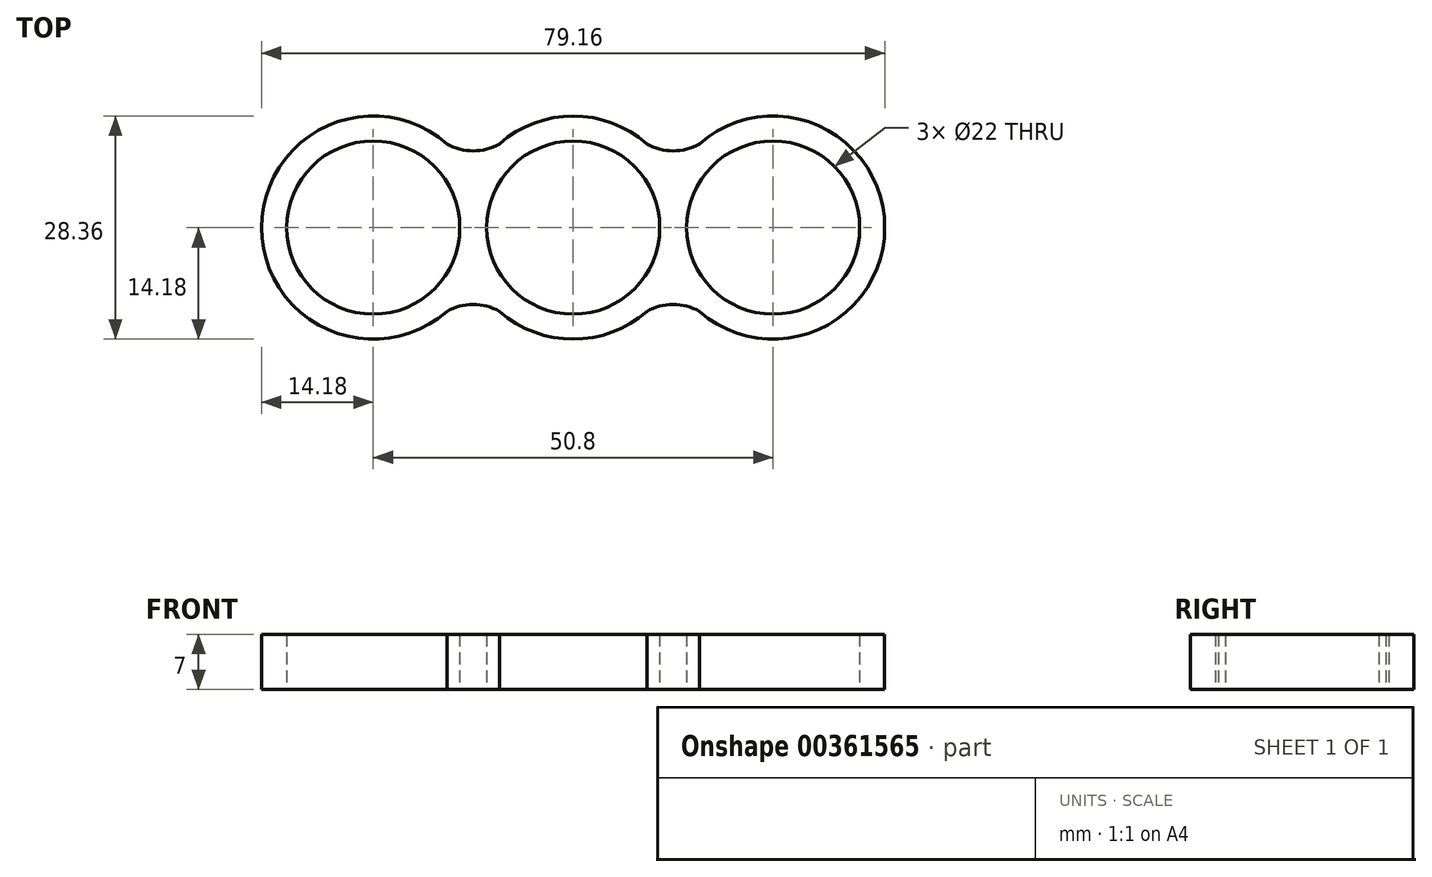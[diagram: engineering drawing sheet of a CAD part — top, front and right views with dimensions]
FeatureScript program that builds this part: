
annotation { "Feature Type Name" : "Feature", "Feature Type Description" : "" }
export const myFeature = defineFeature(function(context is Context, id is Id, definition is map)
    precondition{}
    {
        {
            var Q0;
            Q0=qCreatedBy(makeId("Top.planeOp"),FACE);
            var sketch = newSketch(context, id + "F0", { "sketchPlane" : qUnion([Q0])});
            skCircle(sketch, "E0", {"center": v(0, 0) * mm, "radius": 11 * mm});
            skCircle(sketch, "E1", {"center": v(0, 0) * mm, "radius": 14.17 * mm});
            skLineSegment(sketch, "E2", {"start": v(0, 0) * mm, "end": v(-25.4, 0) * mm});
            skLineSegment(sketch, "E3", {"start": v(0, 0) * mm, "end": v(25.4, 0) * mm});
            skCircle(sketch, "E4", {"center": v(-25.4, 0) * mm, "radius": 11 * mm});
            skCircle(sketch, "E5", {"center": v(25.4, 0) * mm, "radius": 11 * mm});
            skCircle(sketch, "E6", {"center": v(25.4, 0) * mm, "radius": 14.17 * mm});
            skCircle(sketch, "E7", {"center": v(-25.4, 0) * mm, "radius": 14.17 * mm});
            skPoint(sketch, "E8", {"position": v(-16.02, 10.63) * mm});
            skPoint(sketch, "E9", {"position": v(-9.36, 10.64) * mm});
            skPoint(sketch, "E10", {"position": v(16.04, -10.64) * mm});
            skPoint(sketch, "E11", {"position": v(9.36, -10.64) * mm});
            skPoint(sketch, "E12", {"position": v(-12.7, 9.74) * mm});
            skArc(sketch, "E13", {"start": v(-16.02, 10.63) * mm, "mid": v(-12.7, 9.74) * mm, "end": v(-9.36, 10.64) * mm});
            skPoint(sketch, "E14", {"position": v(9.36, 10.64) * mm});
            skPoint(sketch, "E15", {"position": v(16.04, 10.64) * mm});
            skPoint(sketch, "E16", {"position": v(12.7, -9.75) * mm});
            skPoint(sketch, "E17", {"position": v(12.7, 9.75) * mm});
            skPoint(sketch, "E18", {"position": v(-16.04, -10.64) * mm});
            skPoint(sketch, "E19", {"position": v(-9.36, -10.64) * mm});
            skPoint(sketch, "E20", {"position": v(-12.7, -9.75) * mm});
            skArc(sketch, "E21", {"start": v(-9.36, -10.64) * mm, "mid": v(-12.7, -9.75) * mm, "end": v(-16.04, -10.64) * mm});
            skArc(sketch, "E22", {"start": v(16.04, -10.64) * mm, "mid": v(12.7, -9.75) * mm, "end": v(9.36, -10.64) * mm});
            skArc(sketch, "E23", {"start": v(9.36, 10.64) * mm, "mid": v(12.7, 9.75) * mm, "end": v(16.04, 10.64) * mm});
            skSolve(sketch);
        }
        {
            var Q0;
            Q0=makeQuery(id+"F0.imprint","IMPRINT",FACE,{"disambiguationData":[TD([[makeQuery(id+"F0.imprint","IMPRINT",EDGE,{"derivedFrom":sQuery(id+"F0.wireOp",EDGE,"E4")}),-1.0]])]});
            var Q1;
            {var subQ7=sQuery(id+"F0.wireOp",EDGE,"E2");var subQ10=sQuery(id+"F0.wireOp",EDGE,"E0");var subQ13=makeQuery(id+"F0.imprint","INTERSECT",VERTEX,{"derivedFrom":[subQ10,subQ7]});Q1=makeQuery(id+"F0.imprint","IMPRINT",FACE,{"disambiguationData":[TD([[makeQuery(id+"F0.imprint","IMPRINT",EDGE,{"disambiguationData":[TD([[subQ13,1.0]])],"derivedFrom":subQ10}),-1.0]])]});}
            var Q2;
            {var subQ0=sQuery(id+"F0.wireOp",EDGE,"E13");Q2=makeQuery(id+"F0.imprint","IMPRINT",FACE,{"disambiguationData":[TD([[makeQuery(id+"F0.imprint","IMPRINT",EDGE,{"derivedFrom":subQ0}),-1.0]])]});}
            var Q3;
            {var subQ0=sQuery(id+"F0.wireOp",EDGE,"E2");var subQ1=sQuery(id+"F0.wireOp",EDGE,"E1");var subQ2=makeQuery(id+"F0.imprint","INTERSECT",VERTEX,{"derivedFrom":[subQ1,subQ0]});Q3=makeQuery(id+"F0.imprint","IMPRINT",FACE,{"disambiguationData":[TD([[makeQuery(id+"F0.imprint","IMPRINT",EDGE,{"disambiguationData":[TD([[subQ2,1.0]])],"derivedFrom":subQ1}),1.0]])]});}
            var Q4;
            {var subQ0=sQuery(id+"F0.wireOp",EDGE,"E2");var subQ1=sQuery(id+"F0.wireOp",EDGE,"E1");var subQ2=makeQuery(id+"F0.imprint","INTERSECT",VERTEX,{"derivedFrom":[subQ1,subQ0]});Q4=makeQuery(id+"F0.imprint","IMPRINT",FACE,{"disambiguationData":[TD([[makeQuery(id+"F0.imprint","IMPRINT",EDGE,{"disambiguationData":[TD([[subQ2,-1.0]])],"derivedFrom":subQ1}),1.0]])]});}
            var Q5;
            {var subQ7=sQuery(id+"F0.wireOp",EDGE,"E2");var subQ8=sQuery(id+"F0.wireOp",EDGE,"E0");var subQ9=makeQuery(id+"F0.imprint","INTERSECT",VERTEX,{"derivedFrom":[subQ8,subQ7]});Q5=makeQuery(id+"F0.imprint","IMPRINT",FACE,{"disambiguationData":[TD([[makeQuery(id+"F0.imprint","IMPRINT",EDGE,{"disambiguationData":[TD([[subQ9,-1.0]])],"derivedFrom":subQ8}),-1.0]])]});}
            var Q6;
            {var subQ0=sQuery(id+"F0.wireOp",EDGE,"E21");Q6=makeQuery(id+"F0.imprint","IMPRINT",FACE,{"disambiguationData":[TD([[makeQuery(id+"F0.imprint","IMPRINT",EDGE,{"derivedFrom":subQ0}),-1.0]])]});}
            var Q7;
            {var subQ0=sQuery(id+"F0.wireOp",EDGE,"E22");Q7=makeQuery(id+"F0.imprint","IMPRINT",FACE,{"disambiguationData":[TD([[makeQuery(id+"F0.imprint","IMPRINT",EDGE,{"derivedFrom":subQ0}),-1.0]])]});}
            var Q8;
            Q8=makeQuery(id+"F0.imprint","IMPRINT",FACE,{"disambiguationData":[TD([[makeQuery(id+"F0.imprint","IMPRINT",EDGE,{"derivedFrom":sQuery(id+"F0.wireOp",EDGE,"E5")}),-1.0]])]});
            var Q9;
            {var subQ0=sQuery(id+"F0.wireOp",EDGE,"E3");var subQ1=sQuery(id+"F0.wireOp",EDGE,"E1");var subQ2=makeQuery(id+"F0.imprint","INTERSECT",VERTEX,{"derivedFrom":[subQ1,subQ0]});Q9=makeQuery(id+"F0.imprint","IMPRINT",FACE,{"disambiguationData":[TD([[makeQuery(id+"F0.imprint","IMPRINT",EDGE,{"disambiguationData":[TD([[subQ2,1.0]])],"derivedFrom":subQ1}),1.0]])]});}
            var Q10;
            {var subQ0=sQuery(id+"F0.wireOp",EDGE,"E3");var subQ1=sQuery(id+"F0.wireOp",EDGE,"E1");var subQ2=makeQuery(id+"F0.imprint","INTERSECT",VERTEX,{"derivedFrom":[subQ1,subQ0]});Q10=makeQuery(id+"F0.imprint","IMPRINT",FACE,{"disambiguationData":[TD([[makeQuery(id+"F0.imprint","IMPRINT",EDGE,{"disambiguationData":[TD([[subQ2,-1.0]])],"derivedFrom":subQ1}),1.0]])]});}
            var Q11;
            {var subQ0=sQuery(id+"F0.wireOp",EDGE,"E23");Q11=makeQuery(id+"F0.imprint","IMPRINT",FACE,{"disambiguationData":[TD([[makeQuery(id+"F0.imprint","IMPRINT",EDGE,{"derivedFrom":subQ0}),-1.0]])]});}
            extrude(context, id + "F1", {"entities" : qUnion([Q0, Q1, Q2, Q3, Q4, Q5, Q6, Q7, Q8, Q9, Q10, Q11]), "depth" : 7 * mm});
        }
    });
